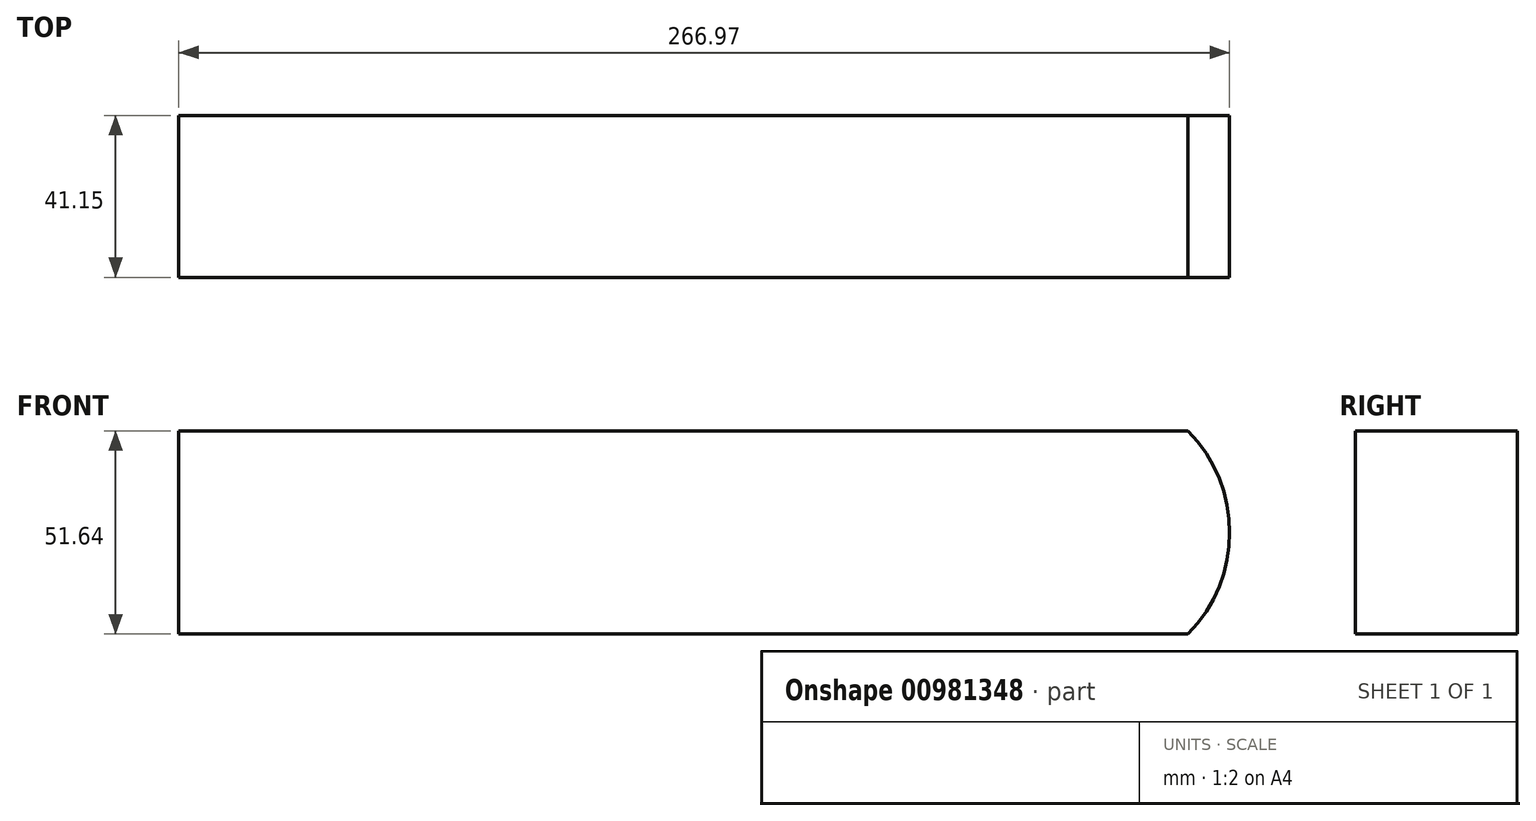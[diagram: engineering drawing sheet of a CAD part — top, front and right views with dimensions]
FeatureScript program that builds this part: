
annotation { "Feature Type Name" : "Feature", "Feature Type Description" : "" }
export const myFeature = defineFeature(function(context is Context, id is Id, definition is map)
    precondition{}
    {
        {
            var Q0;
            Q0=qCreatedBy(makeId("Front.planeOp"),FACE);
            var sketch = newSketch(context, id + "F0", { "sketchPlane" : qUnion([Q0])});
            skLineSegment(sketch, "E0.bottom", {"start": v(-133.43, 29.2) * mm, "end": v(123.02, 29.2) * mm});
            skLineSegment(sketch, "E0.top", {"start": v(-133.43, -22.43) * mm, "end": v(123.02, -22.43) * mm});
            skLineSegment(sketch, "E0.left", {"start": v(-133.43, 29.2) * mm, "end": v(-133.43, -22.43) * mm});
            skLineSegment(sketch, "E0.right", {"start": v(123.02, 29.2) * mm, "end": v(123.02, -22.43) * mm});
            skArc(sketch, "E1", {"start": v(123.02, 29.2) * mm, "mid": v(63.22, -12.36) * mm, "end": v(133.33, 7.33) * mm});
            skArc(sketch, "E2", {"start": v(133.33, 7.33) * mm, "mid": v(61.73, 15.48) * mm, "end": v(123.02, -22.43) * mm});
            skLineSegment(sketch, "E3", {"start": v(-130.44, -32.75) * mm, "end": v(-78.81, -28.46) * mm});
            skSolve(sketch);
        }
        {
            var Q0;
            {var subQ0=sQuery(id+"F0.wireOp",EDGE,"E0.left");Q0=makeQuery(id+"F0.imprint","IMPRINT",FACE,{"disambiguationData":[TD([[makeQuery(id+"F0.imprint","IMPRINT",EDGE,{"derivedFrom":subQ0}),1.0]])]});}
            var Q1;
            {var subQ1=sQuery(id+"F0.wireOp",EDGE,"E0.right");Q1=makeQuery(id+"F0.imprint","IMPRINT",FACE,{"disambiguationData":[TD([[makeQuery(id+"F0.imprint","IMPRINT",EDGE,{"derivedFrom":subQ1}),-1.0]])]});}
            var Q2;
            {var subQ0=sQuery(id+"F0.wireOp",EDGE,"E0.right");Q2=makeQuery(id+"F0.imprint","IMPRINT",FACE,{"disambiguationData":[TD([[makeQuery(id+"F0.imprint","IMPRINT",EDGE,{"derivedFrom":subQ0}),1.0]])]});}
            extrude(context, id + "F1", {"entities" : qUnion([Q0, Q1, Q2]), "depth" : 41.15 * mm, "offsetDistance" : 25.4 * mm});
        }
    });
